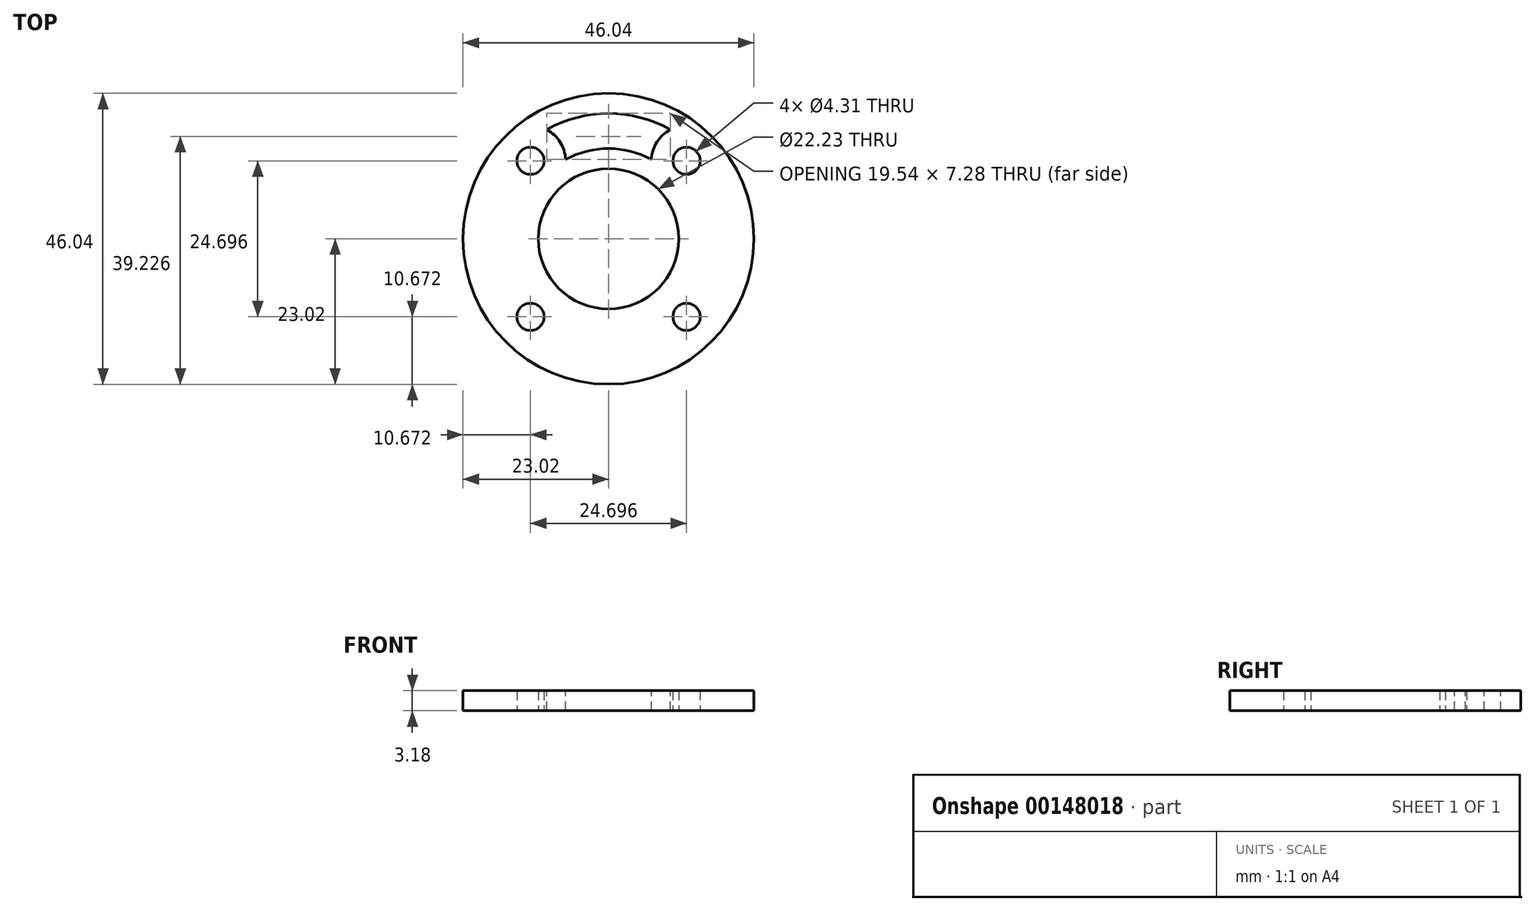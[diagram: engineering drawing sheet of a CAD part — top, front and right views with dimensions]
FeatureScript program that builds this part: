
annotation { "Feature Type Name" : "Feature", "Feature Type Description" : "" }
export const myFeature = defineFeature(function(context is Context, id is Id, definition is map)
    precondition{}
    {
        {
            var Q0;
            Q0=qCreatedBy(makeId("Top.planeOp"),FACE);
            var sketch = newSketch(context, id + "F0", { "sketchPlane" : qUnion([Q0])});
            skCircle(sketch, "E0", {"center": v(0, 0) * mm, "radius": 23.02 * mm});
            skCircle(sketch, "E1", {"center": v(0, 0) * mm, "radius": 11.11 * mm});
            skLineSegment(sketch, "E2.bottom", {"start": v(-12.35, 12.35) * mm, "end": v(12.35, 12.35) * mm, "construction": true});
            skLineSegment(sketch, "E2.top", {"start": v(-12.35, -12.35) * mm, "end": v(12.35, -12.35) * mm, "construction": true});
            skLineSegment(sketch, "E2.left", {"start": v(-12.35, 12.35) * mm, "end": v(-12.35, -12.35) * mm, "construction": true});
            skLineSegment(sketch, "E2.right", {"start": v(12.35, 12.35) * mm, "end": v(12.35, -12.35) * mm, "construction": true});
            skCircle(sketch, "E3", {"center": v(12.35, 12.35) * mm, "radius": 2.15 * mm});
            skCircle(sketch, "E4", {"center": v(-12.35, 12.35) * mm, "radius": 2.15 * mm});
            skCircle(sketch, "E5", {"center": v(-12.35, -12.35) * mm, "radius": 2.15 * mm});
            skCircle(sketch, "E6", {"center": v(12.35, -12.35) * mm, "radius": 2.15 * mm});
            skSolve(sketch);
        }
        {
            var Q0;
            Q0=qSketchRegion(id+"F0",true);
            extrude(context, id + "F1", {"entities" : qUnion([Q0]), "depth" : 3.17 * mm});
        }
        {
            var Q0;
            Q0=makeQuery(id+"F1.opExtrude","CAP_FACE",FACE,{"disambiguationData":[OSD([sQuery(id+"F0.wireOp",EDGE,"E0"),sQuery(id+"F0.wireOp",EDGE,"E1"),sQuery(id+"F0.wireOp",EDGE,"E3"),sQuery(id+"F0.wireOp",EDGE,"E4"),sQuery(id+"F0.wireOp",EDGE,"E5"),sQuery(id+"F0.wireOp",EDGE,"E6")])],"isStart":false});
            var sketch = newSketch(context, id + "F2", { "sketchPlane" : qUnion([Q0])});
            skArc(sketch, "E7", {"start": v(-6.8, 12.57) * mm, "mid": v(-7.65, 15.32) * mm, "end": v(-9.77, 17.27) * mm});
            skArc(sketch, "E8", {"start": v(9.77, 17.27) * mm, "mid": v(7.65, 15.32) * mm, "end": v(6.8, 12.57) * mm});
            skArc(sketch, "E9", {"start": v(9.77, 17.27) * mm, "mid": v(0, 19.84) * mm, "end": v(-9.77, 17.27) * mm});
            skArc(sketch, "E10", {"start": v(6.8, 12.57) * mm, "mid": v(0, 14.29) * mm, "end": v(-6.8, 12.57) * mm});
            skSolve(sketch);
        }
        {
            var Q0;
            Q0=makeQuery(id+"F2.imprint","IMPRINT",FACE,{"disambiguationData":[TD([[makeQuery(id+"F2.imprint","IMPRINT",EDGE,{"derivedFrom":sQuery(id+"F2.wireOp",EDGE,"E7")}),-1.0]])]});
            var Q1;
            Q1=makeQuery(id+"F1.opExtrude","CAP_FACE",FACE,{"disambiguationData":[OSD([sQuery(id+"F0.wireOp",EDGE,"E0"),sQuery(id+"F0.wireOp",EDGE,"E1"),sQuery(id+"F0.wireOp",EDGE,"E3"),sQuery(id+"F0.wireOp",EDGE,"E4"),sQuery(id+"F0.wireOp",EDGE,"E5"),sQuery(id+"F0.wireOp",EDGE,"E6")])],"isStart":true});
            extrude(context, id + "F3", {"entities" : qUnion([Q0]), "operationType" : NewBodyOperationType.REMOVE, "endBound" : BoundingType.UP_TO_SURFACE, "oppositeDirection" : true, "endBoundEntityFace" : qUnion([Q1]), "depth" : 25.4 * mm});
        }
    });
